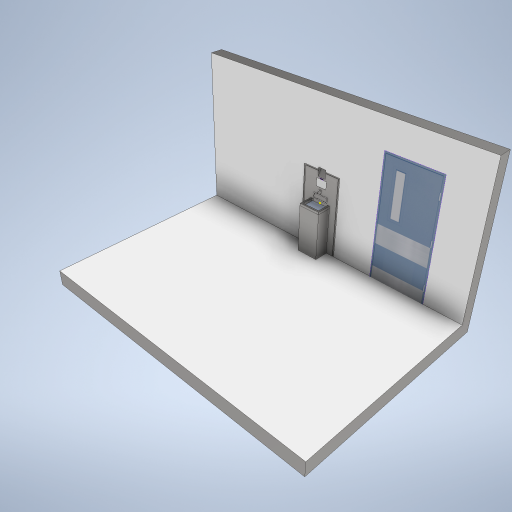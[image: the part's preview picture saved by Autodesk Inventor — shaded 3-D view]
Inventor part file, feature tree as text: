
AUTODESK INVENTOR PART (.ipt)
format: ipt  version: 2024.2 (Build 282272000, 272)  size: 1,664,512 bytes
history: native  units: in
note: dims shown in document units (in); Inventor stores cm internally (conversion verified against a paired STEP export)
features: sketch x20, extrude x14, other x5, plane x2, mirror x1
ambient origin geometry x8: Origin, YZ Plane, XZ Plane, XY Plane, X Axis, Y Axis, Z Axis, Center Point
bodies: Solid2 (feature_tree), Solid1 (feature_tree)
feature tree (42):
  extrude  "Extrusion2"  Depth=13.0in TaperAngle=0.0deg
  extrude  "Extrusion3"  TaperAngle=0.0deg  [1 undecoded]
  extrude  "Extrusion4"  Depth=0.6181in
  extrude  "Extrusion5"  Depth=0.5in
  extrude  "Extrusion6"  Depth=2.5in
  extrude  "Extrusion7"  Depth=0.9in
  extrude  "Extrusion8"  Depth=6.3386in
  extrude  "Extrusion9"  Depth=4.2in
  plane  "Work Plane1"
  mirror  "Mirror1"
  sketch  "Sketch11"  dims[d22=5.5in d23=1.0in d24=0.0in]
  extrude  "Extrusion10"  Depth=1.0in TaperAngle=0.0deg
  extrude  "Extrusion11"  Depth=100.0in
  sketch  "Sketch14"  dims[d33=10.0in d34=0.0in d35=0.3937in d36=0.0in]
  extrude  "Extrusion12"  Depth=100.0in
  sketch  "Sketch16"  dims[d41=12.0187in d42=0.0in d43=10.0in d44=0.0in]
  extrude  "Extrusion13"  Depth=0.3937in TaperAngle=0.0deg
  sketch  "Sketch18"  dims[d58=0.5in d59=0.0in]
  sketch  "Sketch19"  dims[d72=0.5in d73=0.0in]
  plane  "Work Plane2"
  extrude  "Extrusion15"  Depth=157.4803in
  sketch  "Sketch22"  dims[d109=0.01in d110=0.0in]
  extrude  "Extrusion16"  Depth=10.0in TaperAngle=0.0deg
  sketch  "Sketch2"  dims[d2=1.5625in d3=0.0in d4=13.0in d5=0.0in]
  sketch  "Sketch3"  dims[d6=0.5in d7=0.0in]
  sketch  "Sketch4"  dims[d8=0.5in d9=0.6181in]
  sketch  "Sketch5"  dims[d10=0.5in d11=0.5in]
  sketch  "Sketch7"  dims[d12=0.5in d13=2.5in]
  sketch  "Sketch8"  dims[d14=2.5in d15=0.9in]
  sketch  "Sketch9"  dims[d16=1.0in d17=0.0in d19=6.3386in]
  sketch  "Sketch10"  dims[d20=4.2in d21=4.2in]
  sketch  "Sketch12"  dims[d29=39.3701in d30=100.0in]
  sketch  "Sketch13"  dims[d31=118.1102in d32=100.0in]
  other  "Image1"
  sketch  "Sketch15"  dims[d38=12.0187in d39=0.0in d40=157.4803in]
  other  "Image2"
  other  "Image3"
  sketch  "Sketch17"  dims[d45=10.0in d46=0.0in]
  other  "Image4"
  other  "Image5"
  sketch  "Sketch21"  dims[d100=6.3125in d101=0.0in]
  sketch  "Sketch23"  dims[d60=0.5in d61=1.9685in]
note: 1 required parameter value undecoded (feature->parameter linkage not recoverable at this tier; creation-order binding heuristic only, values carry confidence <= 0.55)
